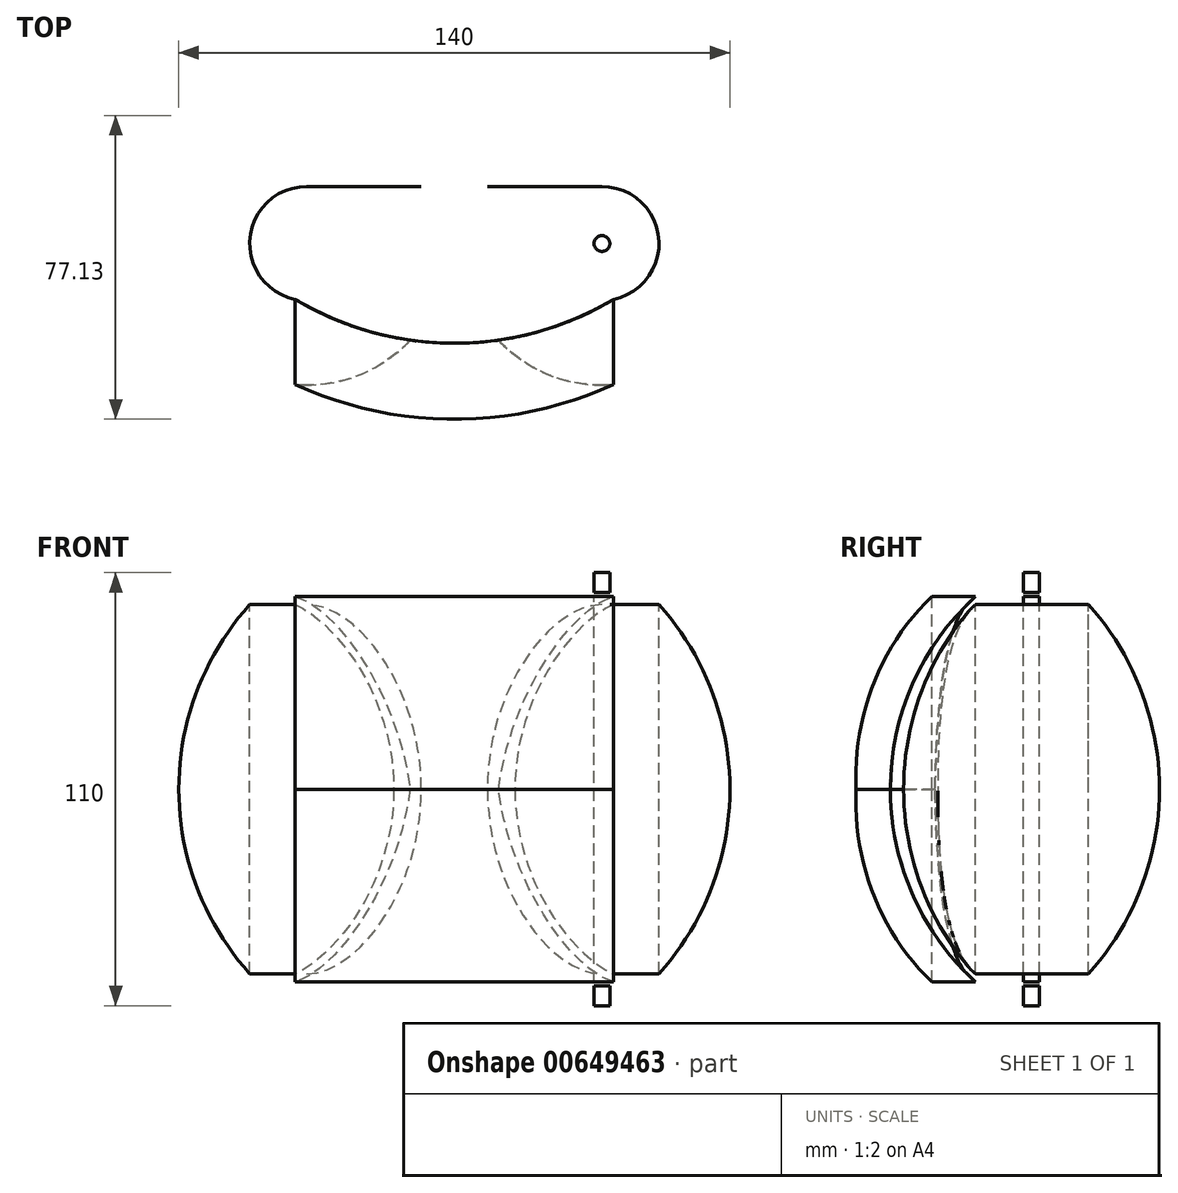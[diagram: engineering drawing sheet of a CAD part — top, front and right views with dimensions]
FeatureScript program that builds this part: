
annotation { "Feature Type Name" : "Feature", "Feature Type Description" : "" }
export const myFeature = defineFeature(function(context is Context, id is Id, definition is map)
    precondition{}
    {
        {
            var Q0;
            Q0=qCreatedBy(makeId("Front.planeOp"),FACE);
            var sketch = newSketch(context, id + "F0", { "sketchPlane" : qUnion([Q0])});
            skCircle(sketch, "E0", {"center": v(0, 0) * mm, "radius": 75 * mm, "construction": true});
            skLineSegment(sketch, "E1", {"start": v(-37.5, 72.95) * mm, "end": v(-37.5, -72.39) * mm, "construction": true});
            skLineSegment(sketch, "E2.MirrorCS", {"start": v(37.5, 72.95) * mm, "end": v(37.5, -72.39) * mm, "construction": true});
            skArc(sketch, "E3", {"start": v(70, 0) * mm, "mid": v(64.8, 26.46) * mm, "end": v(50, 49) * mm});
            skArc(sketch, "E4.MirrorCS", {"start": v(70, 0) * mm, "mid": v(64.8, -26.46) * mm, "end": v(50, -49) * mm});
            skLineSegment(sketch, "E5", {"start": v(50, 49) * mm, "end": v(37.5, 49) * mm});
            skLineSegment(sketch, "E6", {"start": v(50, -49) * mm, "end": v(37.5, -49) * mm});
            skLineSegment(sketch, "E7", {"start": v(37.5, -49) * mm, "end": v(37.5, 49) * mm});
            skSolve(sketch);
        }
        {
            var Q0;
            Q0=makeQuery(id+"F0.imprint","IMPRINT",FACE,{"disambiguationData":[TD([[makeQuery(id+"F0.imprint","IMPRINT",EDGE,{"derivedFrom":sQuery(id+"F0.wireOp",EDGE,"E3")}),1.0]])]});
            var Q1;
            Q1=sQuery(id+"F0.wireOp",EDGE,"E2.MirrorCS");
            revolve(context, id + "F1", {"entities" : qUnion([Q0]), "axis" : qUnion([Q1]), "revolveType" : RevolveType.FULL});
        }
        {
            var Q0;
            Q0=makeQuery(id+"F1.opRevolve","SWEPT_BODY",BODY,{"disambiguationData":[OSD([sQuery(id+"F0.wireOp",EDGE,"E3"),sQuery(id+"F0.wireOp",EDGE,"E4.MirrorCS"),sQuery(id+"F0.wireOp",EDGE,"E5"),sQuery(id+"F0.wireOp",EDGE,"E6"),sQuery(id+"F0.wireOp",EDGE,"E7")])]});
            var Q1;
            Q1=qCreatedBy(makeId("Right.planeOp"),FACE);
            mirror(context, id + "F2", {"entities" : qUnion([Q0]), "mirrorPlane" : qUnion([Q1])});
        }
        {
            var Q0;
            Q0=makeQuery(id+"F2.opPattern","COPY",FACE,{"derivedFrom":makeQuery(id+"F1.opRevolve","SWEPT_FACE",FACE,{"disambiguationData":[OSD([sQuery(id+"F0.wireOp",EDGE,"E5")])]}),"instanceName":"1"});
            var sketch = newSketch(context, id + "F3", { "sketchPlane" : qUnion([Q0])});
            skArc(sketch, "E8", {"start": v(-40.42, -14.2) * mm, "mid": v(-28.34, -11.23) * mm, "end": v(-23, 0) * mm});
            skArc(sketch, "E9.MirrorCS", {"start": v(40.42, -14.2) * mm, "mid": v(28.34, -11.23) * mm, "end": v(23, 0) * mm});
            skArc(sketch, "E10", {"start": v(-40.42, -14.2) * mm, "mid": v(0, -25.34) * mm, "end": v(40.42, -14.2) * mm});
            skLineSegment(sketch, "E11", {"start": v(23, 0) * mm, "end": v(-23, 0) * mm});
            skSolve(sketch);
        }
        {
            var Q0;
            Q0=qCreatedBy(makeId("Top.planeOp"),FACE);
            var sketch = newSketch(context, id + "F4", { "sketchPlane" : qUnion([Q0])});
            skLineSegment(sketch, "E12", {"start": v(40.42, -49.94) * mm, "end": v(40.42, 28.63) * mm, "construction": true});
            skArc(sketch, "E13", {"start": v(1.53, 0) * mm, "mid": v(13.12, -26.45) * mm, "end": v(40.42, -35.85) * mm});
            skArc(sketch, "E14.MirrorCS", {"start": v(-1.53, 0) * mm, "mid": v(-13.12, -26.45) * mm, "end": v(-40.42, -35.85) * mm});
            skArc(sketch, "E15", {"start": v(-40.42, -35.85) * mm, "mid": v(0, -44.56) * mm, "end": v(40.42, -35.85) * mm});
            skLineSegment(sketch, "E16", {"start": v(-1.53, 0) * mm, "end": v(1.53, 0) * mm});
            skSolve(sketch);
        }
        {
            var Q0;
            Q0=qCreatedBy(makeId("Right.planeOp"),FACE);
            cPlane(context, id + "F5", {"entities" : qUnion([Q0]), "cplaneType" : CPlaneType.OFFSET, "offset" : 40.42 * mm, "oppositeDirection" : true, "width" : 150 * mm, "height" : 150 * mm});
        }
        {
            var Q0;
            Q0=qCreatedBy(id+"F5.planeOp",FACE);
            var sketch = newSketch(context, id + "F6", { "sketchPlane" : qUnion([Q0])});
            skArc(sketch, "E17", {"start": v(-14.2, 49) * mm, "mid": v(-30.2, 26.79) * mm, "end": v(-35.85, 0) * mm});
            skSolve(sketch);
        }
        {
            var Q0;
            Q0=qCreatedBy(makeId("Front.planeOp"),FACE);
            var sketch = newSketch(context, id + "F7", { "sketchPlane" : qUnion([Q0])});
            skArc(sketch, "E18", {"start": v(-1.53, 0) * mm, "mid": v(-7.13, 26.75) * mm, "end": v(-23, 49) * mm});
            skArc(sketch, "E19.MirrorCS", {"start": v(1.53, 0) * mm, "mid": v(7.13, 26.75) * mm, "end": v(23, 49) * mm});
            skSolve(sketch);
        }
        {
            var Q0;
            Q0=qCreatedBy(makeId("Right.planeOp"),FACE);
            cPlane(context, id + "F8", {"entities" : qUnion([Q0]), "cplaneType" : CPlaneType.OFFSET, "offset" : 40.42 * mm, "width" : 150 * mm, "height" : 150 * mm});
        }
        {
            var Q0;
            Q0=qCreatedBy(id+"F8.planeOp",FACE);
            var sketch = newSketch(context, id + "F9", { "sketchPlane" : qUnion([Q0])});
            skArc(sketch, "E20", {"start": v(-14.2, 49) * mm, "mid": v(-30.2, 26.79) * mm, "end": v(-35.85, 0) * mm});
            skSolve(sketch);
        }
        {
            var Q0;
            Q0=makeQuery(id+"F3.imprint","IMPRINT",FACE,{"disambiguationData":[TD([[makeQuery(id+"F3.imprint","IMPRINT",EDGE,{"derivedFrom":sQuery(id+"F3.wireOp",EDGE,"E8")}),-1.0]])]});
            var Q1;
            Q1=makeQuery(id+"F4.imprint","IMPRINT",FACE,{"disambiguationData":[TD([[makeQuery(id+"F4.imprint","IMPRINT",EDGE,{"derivedFrom":sQuery(id+"F4.wireOp",EDGE,"E13")}),-1.0]])]});
            var Q2;
            Q2=sQuery(id+"F7.wireOp",EDGE,"E18");
            var Q3;
            Q3=sQuery(id+"F7.wireOp",EDGE,"E19.MirrorCS");
            var Q4;
            Q4=sQuery(id+"F6.wireOp",EDGE,"E17");
            var Q5;
            Q5=sQuery(id+"F9.wireOp",EDGE,"E20");
            loft(context, id + "F10", {"addGuides" : true, "sheetProfilesArray" : [{ "sheetProfileEntities" : qUnion([Q0]) }, { "sheetProfileEntities" : qUnion([Q1]) }], "guidesArray" : [{ "guideEntities" : qUnion([Q2]), "guideDerivativeType" : LoftGuideDerivativeType.DEFAULT, "guideDerivativeMagnitude" : 1 }, { "guideEntities" : qUnion([Q3]), "guideDerivativeType" : LoftGuideDerivativeType.DEFAULT, "guideDerivativeMagnitude" : 1 }, { "guideEntities" : qUnion([Q4]), "guideDerivativeType" : LoftGuideDerivativeType.DEFAULT, "guideDerivativeMagnitude" : 1 }, { "guideEntities" : qUnion([Q5]), "guideDerivativeType" : LoftGuideDerivativeType.DEFAULT, "guideDerivativeMagnitude" : 1 }]});
        }
        {
            var Q0;
            Q0=makeQuery(id+"F10.opLoft","SWEPT_BODY",BODY,{"disambiguationData":[OSD([makeQuery(id+"F3.imprint","IMPRINT",FACE,{"disambiguationData":[TD([[makeQuery(id+"F3.imprint","IMPRINT",EDGE,{"derivedFrom":sQuery(id+"F3.wireOp",EDGE,"E8")}),-1.0]])]}),makeQuery(id+"F4.imprint","IMPRINT",FACE,{"disambiguationData":[TD([[makeQuery(id+"F4.imprint","IMPRINT",EDGE,{"derivedFrom":sQuery(id+"F4.wireOp",EDGE,"E13")}),-1.0]])]}),sQuery(id+"F6.wireOp",EDGE,"E17"),sQuery(id+"F7.wireOp",EDGE,"E18"),sQuery(id+"F7.wireOp",EDGE,"E19.MirrorCS"),sQuery(id+"F9.wireOp",EDGE,"E20")])]});
            var Q1;
            Q1=qCreatedBy(makeId("Top.planeOp"),FACE);
            mirror(context, id + "F11", {"operationType" : NewBodyOperationType.ADD, "entities" : qUnion([Q0]), "mirrorPlane" : qUnion([Q1])});
        }
        {
            var Q0;
            Q0=makeQuery(id+"F10.opLoft","CAP_FACE",FACE,{"disambiguationData":[OSD([makeQuery(id+"F3.imprint","IMPRINT",FACE,{"disambiguationData":[TD([[makeQuery(id+"F3.imprint","IMPRINT",EDGE,{"derivedFrom":sQuery(id+"F3.wireOp",EDGE,"E8")}),-1.0]])]})])],"isStart":true});
            extrude(context, id + "F12", {"entities" : qUnion([Q0]), "operationType" : NewBodyOperationType.ADD, "depth" : 1 * mm, "offsetDistance" : 25 * mm});
        }
        {
            var Q0;
            Q0=makeQuery(id+"F11.opPattern","COPY",FACE,{"derivedFrom":makeQuery(id+"F10.opLoft","CAP_FACE",FACE,{"disambiguationData":[OSD([makeQuery(id+"F3.imprint","IMPRINT",FACE,{"disambiguationData":[TD([[makeQuery(id+"F3.imprint","IMPRINT",EDGE,{"derivedFrom":sQuery(id+"F3.wireOp",EDGE,"E8")}),-1.0]])]})])],"isStart":true}),"instanceName":"1"});
            extrude(context, id + "F13", {"entities" : qUnion([Q0]), "operationType" : NewBodyOperationType.ADD, "depth" : 1 * mm, "offsetDistance" : 25 * mm});
        }
        {
            var Q0;
            Q0=makeQuery(id+"F12.opExtrude","CAP_FACE",FACE,{"disambiguationData":[OSD([makeQuery(id+"F3.imprint","IMPRINT",FACE,{"disambiguationData":[TD([[makeQuery(id+"F3.imprint","IMPRINT",EDGE,{"derivedFrom":sQuery(id+"F3.wireOp",EDGE,"E8")}),-1.0]])]})])],"isStart":false});
            var sketch = newSketch(context, id + "F14", { "sketchPlane" : qUnion([Q0])});
            skArc(sketch, "E21", {"start": v(-40.42, -14.2) * mm, "mid": v(0, -25.34) * mm, "end": v(40.42, -14.2) * mm});
            skLineSegment(sketch, "E22", {"start": v(-37.5, 14.5) * mm, "end": v(37.5, 14.5) * mm});
            skLineSegment(sketch, "E23", {"start": v(-37.5, 0) * mm, "end": v(-37.5, 22.1) * mm, "construction": true});
            skLineSegment(sketch, "E24", {"start": v(37.5, 0) * mm, "end": v(37.5, 22.92) * mm, "construction": true});
            skArc(sketch, "E25", {"start": v(-37.5, 14.5) * mm, "mid": v(-51.92, 1.47) * mm, "end": v(-40.42, -14.2) * mm});
            skArc(sketch, "E26", {"start": v(40.42, -14.2) * mm, "mid": v(51.92, 1.47) * mm, "end": v(37.5, 14.5) * mm});
            skSolve(sketch);
        }
        {
            var Q0;
            Q0 = qSketchRegion(id + "F14", true);
            extrude(context, id + "F15", {"entities" : qUnion([Q0]), "depth" : 5 * mm, "offsetDistance" : 25 * mm});
        }
        {
            var Q0;
            Q0=makeQuery(id+"F15.opExtrude","SWEPT_BODY",BODY,{"disambiguationData":[OSD([sQuery(id+"F14.wireOp",EDGE,"E21"),sQuery(id+"F14.wireOp",EDGE,"E22"),sQuery(id+"F14.wireOp",EDGE,"E25"),sQuery(id+"F14.wireOp",EDGE,"E26")])]});
            var Q1;
            Q1=qCreatedBy(makeId("Top.planeOp"),FACE);
            mirror(context, id + "F16", {"operationType" : NewBodyOperationType.ADD, "entities" : qUnion([Q0]), "mirrorPlane" : qUnion([Q1])});
        }
        {
            var Q0;
            Q0=makeQuery(id+"F15.opExtrude","CAP_FACE",FACE,{"disambiguationData":[OSD([sQuery(id+"F14.wireOp",EDGE,"E21"),sQuery(id+"F14.wireOp",EDGE,"E22"),sQuery(id+"F14.wireOp",EDGE,"E25"),sQuery(id+"F14.wireOp",EDGE,"E26")])],"isStart":false});
            var sketch = newSketch(context, id + "F17", { "sketchPlane" : qUnion([Q0])});
            skCircle(sketch, "E27", {"center": v(-37.5, 0) * mm, "radius": 2 * mm});
            skCircle(sketch, "E28.MirrorC", {"center": v(37.5, 0) * mm, "radius": 2 * mm});
            skCircle(sketch, "E29", {"center": v(0, -21.03) * mm, "radius": 2 * mm});
            skSolve(sketch);
        }
        {
            var Q0;
            Q0=makeQuery(id+"F17.imprint","IMPRINT",FACE,{"disambiguationData":[TD([[makeQuery(id+"F17.imprint","IMPRINT",EDGE,{"derivedFrom":sQuery(id+"F17.wireOp",EDGE,"E27")}),1.0]])]});
            var Q1;
            Q1=makeQuery(id+"F17.imprint","IMPRINT",FACE,{"disambiguationData":[TD([[makeQuery(id+"F17.imprint","IMPRINT",EDGE,{"derivedFrom":sQuery(id+"F17.wireOp",EDGE,"E28.MirrorC")}),-1.0]])]});
            var Q2;
            Q2=makeQuery(id+"F17.imprint","IMPRINT",FACE,{"disambiguationData":[TD([[makeQuery(id+"F17.imprint","IMPRINT",EDGE,{"derivedFrom":sQuery(id+"F17.wireOp",EDGE,"E29")}),1.0]])]});
            extrude(context, id + "F18", {"entities" : qUnion([Q0, Q1, Q2]), "operationType" : NewBodyOperationType.REMOVE, "oppositeDirection" : true, "depth" : 120 * mm, "offsetDistance" : 25 * mm});
        }
    });
